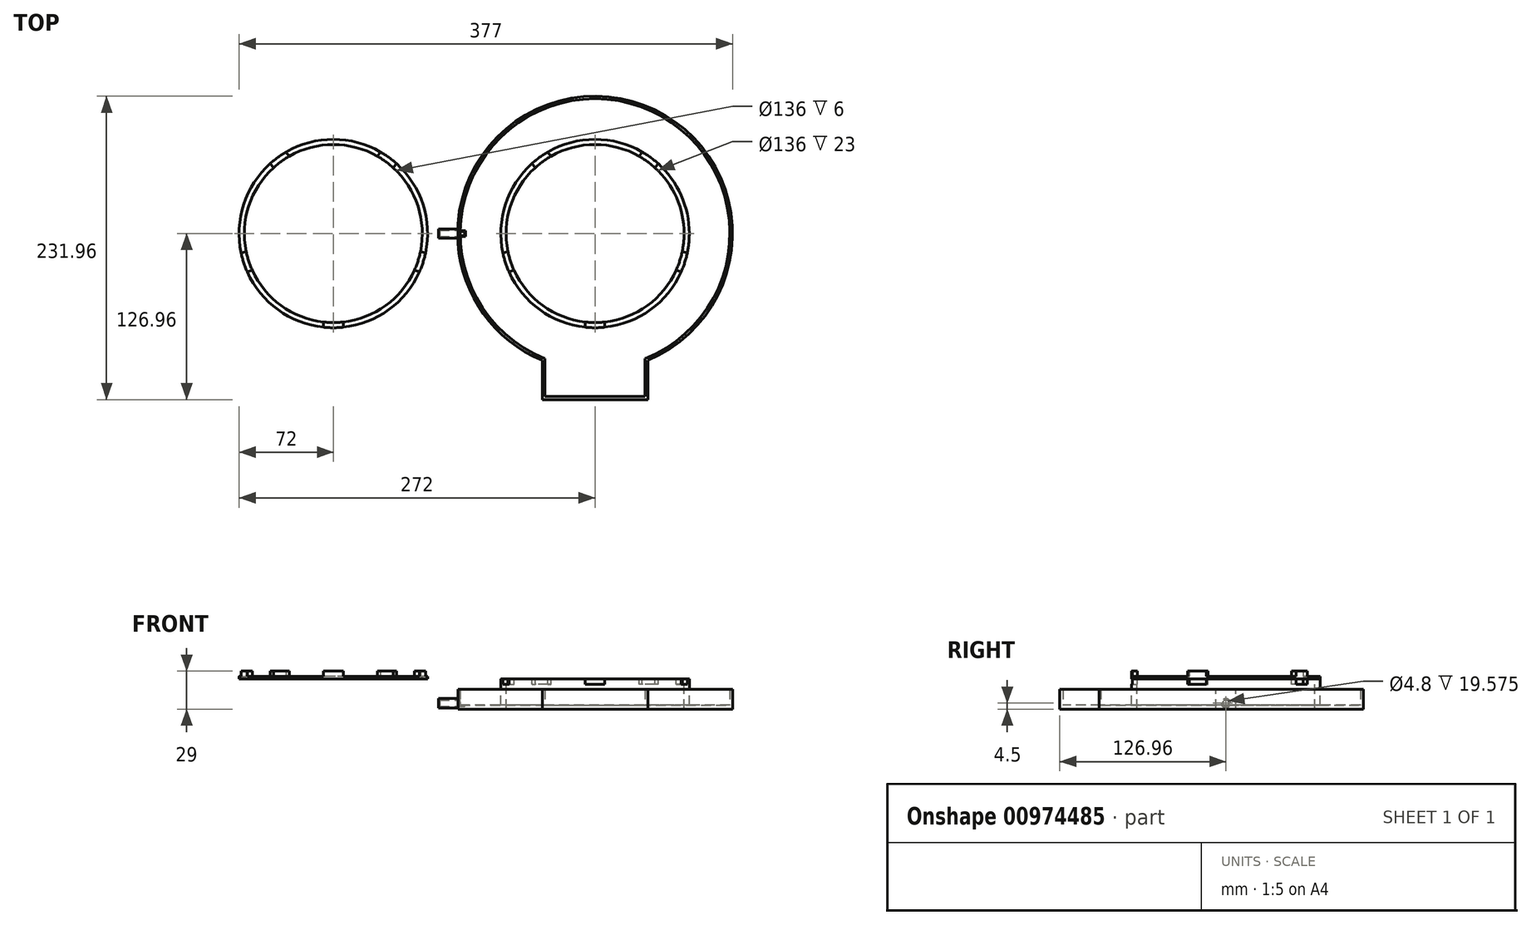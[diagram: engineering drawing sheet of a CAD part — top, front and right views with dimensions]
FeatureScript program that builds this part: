
annotation { "Feature Type Name" : "Feature", "Feature Type Description" : "" }
export const myFeature = defineFeature(function(context is Context, id is Id, definition is map)
    precondition{}
    {
        {
            var Q0;
            Q0=qCreatedBy(makeId("Top.planeOp"),FACE);
            var sketch = newSketch(context, id + "F0", { "sketchPlane" : qUnion([Q0])});
            skCircle(sketch, "E0", {"center": v(0, 0) * mm, "radius": 68 * mm});
            skCircle(sketch, "E1", {"center": v(0, 0) * mm, "radius": 72 * mm});
            skLineSegment(sketch, "E2", {"start": v(-7.5, -71.6) * mm, "end": v(-7.5, -67.59) * mm});
            skLineSegment(sketch, "E3.MirrorCS", {"start": v(7.5, -71.6) * mm, "end": v(7.5, -67.59) * mm});
            skLineSegment(sketch, "E4.1.0", {"start": v(70.42, -15) * mm, "end": v(66.6, -13.75) * mm});
            skLineSegment(sketch, "E4.1.1", {"start": v(65.79, -29.26) * mm, "end": v(61.96, -28.02) * mm});
            skLineSegment(sketch, "E4.2.0", {"start": v(36.02, 62.34) * mm, "end": v(33.66, 59.09) * mm});
            skLineSegment(sketch, "E4.2.1", {"start": v(48.16, 53.52) * mm, "end": v(45.8, 50.27) * mm});
            skLineSegment(sketch, "E4.3.0", {"start": v(-48.16, 53.52) * mm, "end": v(-45.8, 50.27) * mm});
            skLineSegment(sketch, "E4.3.1", {"start": v(-36.02, 62.34) * mm, "end": v(-33.66, 59.09) * mm});
            skLineSegment(sketch, "E4.4.0", {"start": v(-65.79, -29.26) * mm, "end": v(-61.96, -28.02) * mm});
            skLineSegment(sketch, "E4.4.1", {"start": v(-70.42, -15) * mm, "end": v(-66.6, -13.75) * mm});
            skLineSegment(sketch, "E5", {"start": v(-100, -39.03) * mm, "end": v(-100, -29.03) * mm, "construction": true});
            skLineSegment(sketch, "E6.MirrorCS", {"start": v(-192.5, -71.6) * mm, "end": v(-192.5, -67.59) * mm});
            skLineSegment(sketch, "E7.MirrorCS", {"start": v(-151.84, 53.52) * mm, "end": v(-154.2, 50.27) * mm});
            skLineSegment(sketch, "E8.MirrorCS", {"start": v(-265.79, -29.26) * mm, "end": v(-261.96, -28.02) * mm});
            skLineSegment(sketch, "E9.MirrorCS", {"start": v(-207.5, -71.6) * mm, "end": v(-207.5, -67.59) * mm});
            skLineSegment(sketch, "E10.MirrorCS", {"start": v(-163.98, 62.34) * mm, "end": v(-166.34, 59.09) * mm});
            skLineSegment(sketch, "E11.MirrorCS", {"start": v(-270.42, -15) * mm, "end": v(-266.6, -13.75) * mm});
            skLineSegment(sketch, "E12.MirrorCS", {"start": v(-236.02, 62.34) * mm, "end": v(-233.66, 59.09) * mm});
            skLineSegment(sketch, "E13.MirrorCS", {"start": v(-129.58, -15) * mm, "end": v(-133.4, -13.75) * mm});
            skLineSegment(sketch, "E14.MirrorCS", {"start": v(-248.16, 53.52) * mm, "end": v(-245.8, 50.27) * mm});
            skLineSegment(sketch, "E15.MirrorCS", {"start": v(-134.21, -29.26) * mm, "end": v(-138.04, -28.02) * mm});
            skCircle(sketch, "E16.MirrorC", {"center": v(-200, 0) * mm, "radius": 68 * mm});
            skCircle(sketch, "E17.MirrorC", {"center": v(-200, 0) * mm, "radius": 72 * mm});
            skSolve(sketch);
        }
        {
            var Q0;
            {var subQ0=sQuery(id+"F0.wireOp",EDGE,"E4.2.0");Q0=makeQuery(id+"F0.imprint","IMPRINT",FACE,{"disambiguationData":[TD([[makeQuery(id+"F0.imprint","IMPRINT",EDGE,{"derivedFrom":subQ0}),1.0]])]});}
            var Q1;
            {var subQ0=sQuery(id+"F0.wireOp",EDGE,"E4.2.0");Q1=makeQuery(id+"F0.imprint","IMPRINT",FACE,{"disambiguationData":[TD([[makeQuery(id+"F0.imprint","IMPRINT",EDGE,{"derivedFrom":subQ0}),-1.0]])]});}
            var Q2;
            {var subQ0=sQuery(id+"F0.wireOp",EDGE,"E4.3.0");Q2=makeQuery(id+"F0.imprint","IMPRINT",FACE,{"disambiguationData":[TD([[makeQuery(id+"F0.imprint","IMPRINT",EDGE,{"derivedFrom":subQ0}),1.0]])]});}
            var Q3;
            {var subQ0=sQuery(id+"F0.wireOp",EDGE,"E4.3.0");Q3=makeQuery(id+"F0.imprint","IMPRINT",FACE,{"disambiguationData":[TD([[makeQuery(id+"F0.imprint","IMPRINT",EDGE,{"derivedFrom":subQ0}),-1.0]])]});}
            var Q4;
            {var subQ0=sQuery(id+"F0.wireOp",EDGE,"E4.4.0");Q4=makeQuery(id+"F0.imprint","IMPRINT",FACE,{"disambiguationData":[TD([[makeQuery(id+"F0.imprint","IMPRINT",EDGE,{"derivedFrom":subQ0}),1.0]])]});}
            var Q5;
            {var subQ0=sQuery(id+"F0.wireOp",EDGE,"E2");Q5=makeQuery(id+"F0.imprint","IMPRINT",FACE,{"disambiguationData":[TD([[makeQuery(id+"F0.imprint","IMPRINT",EDGE,{"derivedFrom":subQ0}),1.0]])]});}
            var Q6;
            {var subQ0=sQuery(id+"F0.wireOp",EDGE,"E2");Q6=makeQuery(id+"F0.imprint","IMPRINT",FACE,{"disambiguationData":[TD([[makeQuery(id+"F0.imprint","IMPRINT",EDGE,{"derivedFrom":subQ0}),-1.0]])]});}
            var Q7;
            {var subQ0=sQuery(id+"F0.wireOp",EDGE,"E3.MirrorCS");Q7=makeQuery(id+"F0.imprint","IMPRINT",FACE,{"disambiguationData":[TD([[makeQuery(id+"F0.imprint","IMPRINT",EDGE,{"derivedFrom":subQ0}),-1.0]])]});}
            var Q8;
            {var subQ0=sQuery(id+"F0.wireOp",EDGE,"E4.1.0");Q8=makeQuery(id+"F0.imprint","IMPRINT",FACE,{"disambiguationData":[TD([[makeQuery(id+"F0.imprint","IMPRINT",EDGE,{"derivedFrom":subQ0}),1.0]])]});}
            var Q9;
            {var subQ0=sQuery(id+"F0.wireOp",EDGE,"E4.1.0");Q9=makeQuery(id+"F0.imprint","IMPRINT",FACE,{"disambiguationData":[TD([[makeQuery(id+"F0.imprint","IMPRINT",EDGE,{"derivedFrom":subQ0}),-1.0]])]});}
            extrude(context, id + "F1", {"entities" : qUnion([Q0, Q1, Q2, Q3, Q4, Q5, Q6, Q7, Q8, Q9]), "oppositeDirection" : true, "depth" : 23 * mm, "offsetDistance" : 25 * mm});
        }
        {
            var Q0;
            Q0=makeQuery(id+"F1.opExtrude","CAP_FACE",FACE,{"disambiguationData":[OSD([sQuery(id+"F0.wireOp",EDGE,"E0"),sQuery(id+"F0.wireOp",EDGE,"E1")])],"isStart":false});
            var sketch = newSketch(context, id + "F2", { "sketchPlane" : qUnion([Q0])});
            skCircle(sketch, "E18", {"center": v(0, 0) * mm, "radius": 103 * mm});
            skCircle(sketch, "E19", {"center": v(0, 0) * mm, "radius": 105 * mm});
            skLineSegment(sketch, "E20", {"start": v(40.3, 96.96) * mm, "end": v(40.3, 126.96) * mm});
            skLineSegment(sketch, "E21.MirrorCS", {"start": v(-40.3, 96.96) * mm, "end": v(-40.3, 126.96) * mm});
            skLineSegment(sketch, "E22", {"start": v(-38.3, 97.77) * mm, "end": v(-38.3, 124.62) * mm});
            skLineSegment(sketch, "E23", {"start": v(-40.3, 126.96) * mm, "end": v(40.3, 126.96) * mm});
            skLineSegment(sketch, "E24.MirrorCS", {"start": v(38.3, 97.77) * mm, "end": v(38.3, 124.62) * mm});
            skLineSegment(sketch, "E25", {"start": v(-38.3, 124.62) * mm, "end": v(38.3, 124.62) * mm});
            skLineSegment(sketch, "E26", {"start": v(-38.3, 97.77) * mm, "end": v(-38.3, 95.61) * mm});
            skLineSegment(sketch, "E27.MirrorCS", {"start": v(38.3, 97.77) * mm, "end": v(38.3, 95.61) * mm});
            skSolve(sketch);
        }
        {
            var Q0;
            Q0=makeQuery(id+"F2.imprint","IMPRINT",FACE,{"disambiguationData":[TD([[makeQuery(id+"F2.imprint","IMPRINT",EDGE,{"derivedFrom":sQuery(id+"F2.wireOp",EDGE,"E18")}),1.0]])]});
            var Q1;
            {var subQ0=sQuery(id+"F2.wireOp",EDGE,"E22");Q1=makeQuery(id+"F2.imprint","IMPRINT",FACE,{"disambiguationData":[TD([[makeQuery(id+"F2.imprint","IMPRINT",EDGE,{"derivedFrom":subQ0}),-1.0]])]});}
            var Q2;
            {var subQ0=sQuery(id+"F2.wireOp",EDGE,"E26");Q2=makeQuery(id+"F2.imprint","IMPRINT",FACE,{"disambiguationData":[TD([[makeQuery(id+"F2.imprint","IMPRINT",EDGE,{"derivedFrom":subQ0}),1.0]])]});}
            extrude(context, id + "F3", {"entities" : qUnion([Q0, Q1, Q2]), "operationType" : NewBodyOperationType.ADD, "oppositeDirection" : true, "depth" : 3 * mm, "offsetDistance" : 25 * mm});
        }
        {
            var Q0;
            {var subQ3=sQuery(id+"F2.wireOp",EDGE,"E26");Q0=makeQuery(id+"F2.imprint","IMPRINT",FACE,{"disambiguationData":[TD([[makeQuery(id+"F2.imprint","IMPRINT",EDGE,{"derivedFrom":subQ3}),-1.0]])]});}
            var Q1;
            {var subQ0=sQuery(id+"F2.wireOp",EDGE,"E20");Q1=makeQuery(id+"F2.imprint","IMPRINT",FACE,{"disambiguationData":[TD([[makeQuery(id+"F2.imprint","IMPRINT",EDGE,{"derivedFrom":subQ0}),1.0]])]});}
            extrude(context, id + "F4", {"entities" : qUnion([Q0, Q1]), "operationType" : NewBodyOperationType.ADD, "oppositeDirection" : true, "depth" : 15 * mm, "offsetDistance" : 25 * mm});
        }
        {
            var Q0;
            Q0=makeQuery(id+"F4.opExtrude","CAP_FACE",FACE,{"disambiguationData":[OSD([sQuery(id+"F2.wireOp",EDGE,"E18"),sQuery(id+"F2.wireOp",EDGE,"E19"),sQuery(id+"F2.wireOp",EDGE,"E20"),sQuery(id+"F2.wireOp",EDGE,"E21.MirrorCS"),sQuery(id+"F2.wireOp",EDGE,"E22"),sQuery(id+"F2.wireOp",EDGE,"E23"),sQuery(id+"F2.wireOp",EDGE,"E24.MirrorCS"),sQuery(id+"F2.wireOp",EDGE,"E25"),sQuery(id+"F2.wireOp",EDGE,"E26"),sQuery(id+"F2.wireOp",EDGE,"E27.MirrorCS")])],"isStart":false});
            var sketch = newSketch(context, id + "F5", { "sketchPlane" : qUnion([Q0])});
            skLineSegment(sketch, "E28", {"start": v(-104.73, 7.5) * mm, "end": v(-104.73, -7.5) * mm});
            skSolve(sketch);
        }
        {
            var Q0;
            {var subQ0=sQuery(id+"F5.wireOp",EDGE,"E28");Q0=makeQuery(id+"F5.imprint","IMPRINT",FACE,{"disambiguationData":[TD([[makeQuery(id+"F5.imprint","IMPRINT",EDGE,{"derivedFrom":subQ0}),-1.0]])]});}
            extrude(context, id + "F6", {"entities" : qUnion([Q0]), "operationType" : NewBodyOperationType.REMOVE, "oppositeDirection" : true, "depth" : 25 * mm, "offsetDistance" : 25 * mm});
        }
        {
            var Q0;
            Q0=makeQuery(id+"F6.boolean.opBoolean","COPY",FACE,{"derivedFrom":makeQuery(id+"F6.opExtrude","SWEPT_FACE",FACE,{"disambiguationData":[OSD([sQuery(id+"F5.wireOp",EDGE,"E28")])]})});
            var sketch = newSketch(context, id + "F7", { "sketchPlane" : qUnion([Q0])});
            skCircle(sketch, "E29", {"center": v(0, -18.5) * mm, "radius": 2.4 * mm});
            skPoint(sketch, "E29.centerSnap0", {"position": v(0, -23) * mm});
            skCircle(sketch, "E30", {"center": v(0, -18.5) * mm, "radius": 3.5 * mm});
            skSolve(sketch);
        }
        {
            var Q0;
            Q0=makeQuery(id+"F7.imprint","IMPRINT",FACE,{"disambiguationData":[TD([[makeQuery(id+"F7.imprint","IMPRINT",EDGE,{"derivedFrom":sQuery(id+"F7.wireOp",EDGE,"E29")}),-1.0]])]});
            extrude(context, id + "F8", {"entities" : qUnion([Q0]), "operationType" : NewBodyOperationType.ADD, "depth" : 15 * mm, "offsetDistance" : 25 * mm});
        }
        {
            var Q0;
            Q0=makeQuery(id+"F7.imprint","IMPRINT",FACE,{"disambiguationData":[TD([[makeQuery(id+"F7.imprint","IMPRINT",EDGE,{"derivedFrom":sQuery(id+"F7.wireOp",EDGE,"E29")}),1.0]])]});
            extrude(context, id + "F9", {"entities" : qUnion([Q0]), "operationType" : NewBodyOperationType.REMOVE, "oppositeDirection" : true, "depth" : 5 * mm, "offsetDistance" : 25 * mm});
        }
        {
            var Q0;
            Q0=makeQuery(id+"F9.boolean.opBoolean","INTERSECT",EDGE,{"derivedFrom":[makeQuery(id+"F3.opExtrude","CAP_FACE",FACE,{"disambiguationData":[OSD([sQuery(id+"F0.wireOp",EDGE,"E1"),sQuery(id+"F2.wireOp",EDGE,"E18"),sQuery(id+"F2.wireOp",EDGE,"E22"),sQuery(id+"F2.wireOp",EDGE,"E24.MirrorCS"),sQuery(id+"F2.wireOp",EDGE,"E25"),sQuery(id+"F2.wireOp",EDGE,"E26"),sQuery(id+"F2.wireOp",EDGE,"E27.MirrorCS")])],"isStart":false}),makeQuery(id+"F9.opExtrude","CAP_FACE",FACE,{"disambiguationData":[OSD([sQuery(id+"F7.wireOp",EDGE,"E29")])],"isStart":false})]});
            var Q1;
            Q1=makeQuery(id+"F9.boolean.opBoolean","INTERSECT",EDGE,{"disambiguationData":[OD(1.0)],"derivedFrom":[makeQuery(id+"F3.opExtrude","CAP_FACE",FACE,{"disambiguationData":[OSD([sQuery(id+"F0.wireOp",EDGE,"E1"),sQuery(id+"F2.wireOp",EDGE,"E18"),sQuery(id+"F2.wireOp",EDGE,"E22"),sQuery(id+"F2.wireOp",EDGE,"E24.MirrorCS"),sQuery(id+"F2.wireOp",EDGE,"E25"),sQuery(id+"F2.wireOp",EDGE,"E26"),sQuery(id+"F2.wireOp",EDGE,"E27.MirrorCS")])],"isStart":false}),makeQuery(id+"F9.opExtrude","SWEPT_FACE",FACE,{"disambiguationData":[OSD([sQuery(id+"F7.wireOp",EDGE,"E29")])]})]});
            var Q2;
            Q2=makeQuery(id+"F9.boolean.opBoolean","INTERSECT",EDGE,{"disambiguationData":[OD(0.0)],"derivedFrom":[makeQuery(id+"F3.opExtrude","CAP_FACE",FACE,{"disambiguationData":[OSD([sQuery(id+"F0.wireOp",EDGE,"E1"),sQuery(id+"F2.wireOp",EDGE,"E18"),sQuery(id+"F2.wireOp",EDGE,"E22"),sQuery(id+"F2.wireOp",EDGE,"E24.MirrorCS"),sQuery(id+"F2.wireOp",EDGE,"E25"),sQuery(id+"F2.wireOp",EDGE,"E26"),sQuery(id+"F2.wireOp",EDGE,"E27.MirrorCS")])],"isStart":false}),makeQuery(id+"F9.opExtrude","SWEPT_FACE",FACE,{"disambiguationData":[OSD([sQuery(id+"F7.wireOp",EDGE,"E29")])]})]});
            chamfer(context, id + "F10", {"entities" : qUnion([Q0, Q1, Q2]), "width" : .8 * mm, "tangentPropagation" : true});
        }
        {
            var Q0;
            Q0=makeQuery(id+"F8.opExtrude","CAP_EDGE",EDGE,{"disambiguationData":[OSD([sQuery(id+"F7.wireOp",EDGE,"E29")])],"isStart":false});
            chamfer(context, id + "F11", {"entities" : qUnion([Q0]), "width" : 1 * mm, "tangentPropagation" : true});
        }
        {
            var Q0;
            {var subQ0=sQuery(id+"F0.wireOp",EDGE,"E16.MirrorC");var subQ4=makeQuery(id+"F0.imprint","INTERSECT",VERTEX,{"derivedFrom":[sQuery(id+"F0.wireOp",EDGE,"E12.MirrorCS"),subQ0]});Q0=makeQuery(id+"F0.imprint","IMPRINT",FACE,{"disambiguationData":[TD([[makeQuery(id+"F0.imprint","IMPRINT",EDGE,{"disambiguationData":[TD([[subQ4,1.0]])],"derivedFrom":subQ0}),-1.0]])]});}
            var Q1;
            {var subQ0=sQuery(id+"F0.wireOp",EDGE,"E6.MirrorCS");Q1=makeQuery(id+"F0.imprint","IMPRINT",FACE,{"disambiguationData":[TD([[makeQuery(id+"F0.imprint","IMPRINT",EDGE,{"derivedFrom":subQ0}),-1.0]])]});}
            var Q2;
            {var subQ0=sQuery(id+"F0.wireOp",EDGE,"E7.MirrorCS");Q2=makeQuery(id+"F0.imprint","IMPRINT",FACE,{"disambiguationData":[TD([[makeQuery(id+"F0.imprint","IMPRINT",EDGE,{"derivedFrom":subQ0}),1.0]])]});}
            var Q3;
            {var subQ0=sQuery(id+"F0.wireOp",EDGE,"E8.MirrorCS");Q3=makeQuery(id+"F0.imprint","IMPRINT",FACE,{"disambiguationData":[TD([[makeQuery(id+"F0.imprint","IMPRINT",EDGE,{"derivedFrom":subQ0}),-1.0]])]});}
            var Q4;
            {var subQ0=sQuery(id+"F0.wireOp",EDGE,"E11.MirrorCS");Q4=makeQuery(id+"F0.imprint","IMPRINT",FACE,{"disambiguationData":[TD([[makeQuery(id+"F0.imprint","IMPRINT",EDGE,{"derivedFrom":subQ0}),1.0]])]});}
            var Q5;
            {var subQ0=sQuery(id+"F0.wireOp",EDGE,"E10.MirrorCS");Q5=makeQuery(id+"F0.imprint","IMPRINT",FACE,{"disambiguationData":[TD([[makeQuery(id+"F0.imprint","IMPRINT",EDGE,{"derivedFrom":subQ0}),-1.0]])]});}
            extrude(context, id + "F12", {"entities" : qUnion([Q0, Q1, Q2, Q3, Q4, Q5]), "depth" : 2 * mm, "offsetDistance" : 25 * mm});
        }
        {
            var Q0;
            {var subQ0=sQuery(id+"F0.wireOp",EDGE,"E13.MirrorCS");Q0=makeQuery(id+"F0.imprint","IMPRINT",FACE,{"disambiguationData":[TD([[makeQuery(id+"F0.imprint","IMPRINT",EDGE,{"derivedFrom":subQ0}),1.0]])]});}
            var Q1;
            {var subQ0=sQuery(id+"F0.wireOp",EDGE,"E6.MirrorCS");Q1=makeQuery(id+"F0.imprint","IMPRINT",FACE,{"disambiguationData":[TD([[makeQuery(id+"F0.imprint","IMPRINT",EDGE,{"derivedFrom":subQ0}),1.0]])]});}
            var Q2;
            {var subQ0=sQuery(id+"F0.wireOp",EDGE,"E8.MirrorCS");Q2=makeQuery(id+"F0.imprint","IMPRINT",FACE,{"disambiguationData":[TD([[makeQuery(id+"F0.imprint","IMPRINT",EDGE,{"derivedFrom":subQ0}),1.0]])]});}
            var Q3;
            {var subQ0=sQuery(id+"F0.wireOp",EDGE,"E12.MirrorCS");Q3=makeQuery(id+"F0.imprint","IMPRINT",FACE,{"disambiguationData":[TD([[makeQuery(id+"F0.imprint","IMPRINT",EDGE,{"derivedFrom":subQ0}),-1.0]])]});}
            var Q4;
            {var subQ0=sQuery(id+"F0.wireOp",EDGE,"E7.MirrorCS");Q4=makeQuery(id+"F0.imprint","IMPRINT",FACE,{"disambiguationData":[TD([[makeQuery(id+"F0.imprint","IMPRINT",EDGE,{"derivedFrom":subQ0}),-1.0]])]});}
            extrude(context, id + "F13", {"entities" : qUnion([Q0, Q1, Q2, Q3, Q4]), "operationType" : NewBodyOperationType.ADD, "depth" : 6 * mm, "offsetDistance" : 25 * mm});
        }
        {
            var Q0;
            {var subQ0=sQuery(id+"F0.wireOp",EDGE,"E2");Q0=makeQuery(id+"F0.imprint","IMPRINT",FACE,{"disambiguationData":[TD([[makeQuery(id+"F0.imprint","IMPRINT",EDGE,{"derivedFrom":subQ0}),-1.0]])]});}
            var Q1;
            {var subQ0=sQuery(id+"F0.wireOp",EDGE,"E4.4.0");Q1=makeQuery(id+"F0.imprint","IMPRINT",FACE,{"disambiguationData":[TD([[makeQuery(id+"F0.imprint","IMPRINT",EDGE,{"derivedFrom":subQ0}),1.0]])]});}
            var Q2;
            {var subQ0=sQuery(id+"F0.wireOp",EDGE,"E4.3.0");Q2=makeQuery(id+"F0.imprint","IMPRINT",FACE,{"disambiguationData":[TD([[makeQuery(id+"F0.imprint","IMPRINT",EDGE,{"derivedFrom":subQ0}),1.0]])]});}
            var Q3;
            {var subQ0=sQuery(id+"F0.wireOp",EDGE,"E4.2.0");Q3=makeQuery(id+"F0.imprint","IMPRINT",FACE,{"disambiguationData":[TD([[makeQuery(id+"F0.imprint","IMPRINT",EDGE,{"derivedFrom":subQ0}),1.0]])]});}
            var Q4;
            {var subQ0=sQuery(id+"F0.wireOp",EDGE,"E4.1.0");Q4=makeQuery(id+"F0.imprint","IMPRINT",FACE,{"disambiguationData":[TD([[makeQuery(id+"F0.imprint","IMPRINT",EDGE,{"derivedFrom":subQ0}),1.0]])]});}
            extrude(context, id + "F14", {"entities" : qUnion([Q0, Q1, Q2, Q3, Q4]), "operationType" : NewBodyOperationType.REMOVE, "oppositeDirection" : true, "depth" : 4 * mm, "offsetDistance" : 25 * mm});
        }
    });
